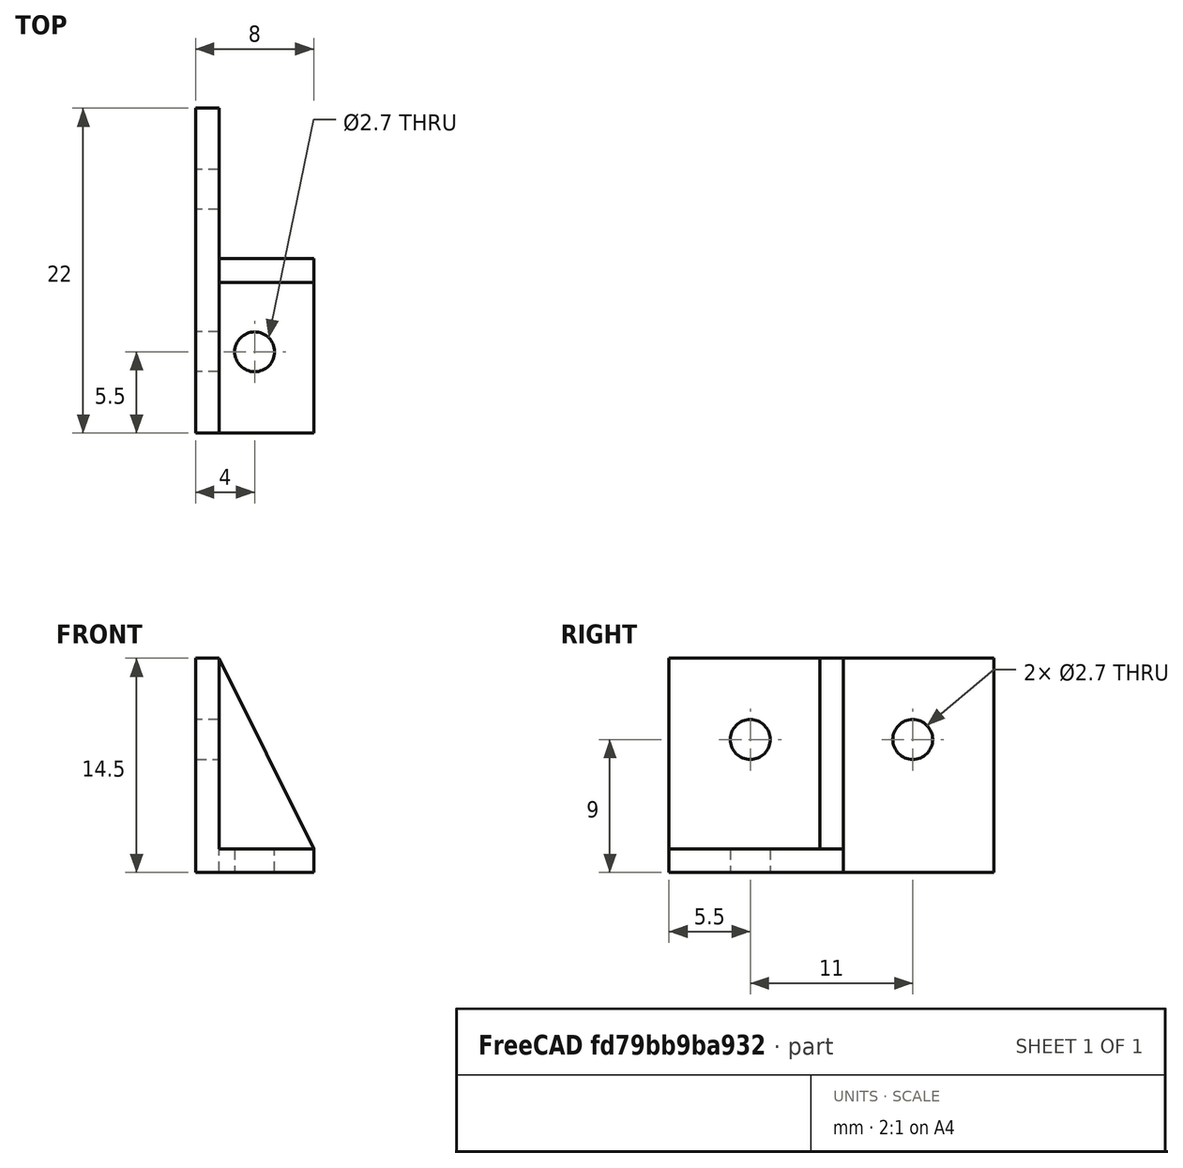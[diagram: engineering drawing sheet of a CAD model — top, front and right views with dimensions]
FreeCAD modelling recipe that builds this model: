
FCSTD DOCUMENT  (FreeCAD 0.20R29410 (Git))
Label: Podule Bracket L
License: All rights reserved
LicenseURL: http://en.wikipedia.org/wiki/All_rights_reserved
objects: Part::Cylinder×3, Part::Cut×3, Part::Box×2, Part::FeaturePython×1, Sketcher::SketchObject×1, Part::Extrusion×1
note: 11 computed .brp shape members not serialized (recipe doc carries the construction recipe); baked Part::Feature solids carry a one-line shape summary decoded from their .brp

FEATURE [Part::Box] Box  label="Cube"
  AttacherType = Attacher::AttachEngine3D
  Height = 14.5
  Length = 1.6
  Width = 22
FEATURE [Part::Cylinder] Cylinder
  Angle = 360
  AttacherType = Attacher::AttachEngine3D
  FirstAngle = 0
  Height = 10
  Placement = pos=(0,5.5,9) rot=(0,1,0;1.5708rad)
  Radius = 1.35
  SecondAngle = 0
FEATURE [Part::Cut] Cut
  Base = -> Box
  Tool = -> Cylinder
FEATURE [Part::Cylinder] Cylinder001
  Angle = 360
  AttacherType = Attacher::AttachEngine3D
  FirstAngle = 0
  Height = 10
  Placement = pos=(0,16.5,9) rot=(0,1,0;1.5708rad)
  Radius = 1.35
  SecondAngle = 0
FEATURE [Part::Cut] Cut001
  Base = -> Cut
  Tool = -> Cylinder001
FEATURE [Part::Box] Box001  label="Cube001"
  AttacherType = Attacher::AttachEngine3D
  Height = 1.6
  Length = 6.4
  Placement = pos=(1.6,0,0) rot=(0,0,1;0rad)
  Width = 11.8
FEATURE [Part::FeaturePython] Connect  # WARN: FeaturePython — macro-defined, semantics opaque (R4)
  Objects = -> [Box001,Cut001]
  Tolerance = 0
FEATURE [Part::Cylinder] Cylinder002
  Angle = 360
  AttacherType = Attacher::AttachEngine3D
  FirstAngle = 0
  Height = 10
  Placement = pos=(4,5.5,0) rot=(0,0,1;0rad)
  Radius = 1.35
  SecondAngle = 0
FEATURE [Part::Cut] Cut002
  Base = -> Connect
  Tool = -> Cylinder002
FEATURE [Sketcher::SketchObject] Sketch
  FullyConstrained = false
  Placement = pos=(0,0,0) rot=(1,0,0;1.5708rad)
  sketch-geometry (3):
    g0: LineSegment StartX=1.59368 StartY=14.4832 StartZ=0 EndX=1.59368 EndY=1.60001 EndZ=0
    g1: LineSegment StartX=1.59368 StartY=1.60001 StartZ=0 EndX=7.99993 EndY=1.60001 EndZ=0
    g2: LineSegment StartX=7.99993 StartY=1.60001 StartZ=0 EndX=1.59368 EndY=14.4832 EndZ=0
  constraints (5):
    c: Vertical(g0)
    c: Coincident(g0,g1)
    c: Horizontal(g1)
    c: Coincident(g1,g2)
    c: Coincident(g2,g0)
FEATURE [Part::Extrusion] Extrude
  Base = -> Sketch
  Dir = (0,-1,-3e-16)
  DirMode = 2
  FaceMakerClass = Part::FaceMakerBullseye
  LengthFwd = 1.6
  LengthRev = 0
  Placement = pos=(0,11.8,0) rot=(0,0,1;0rad)
  Solid = true
  Symmetric = false
